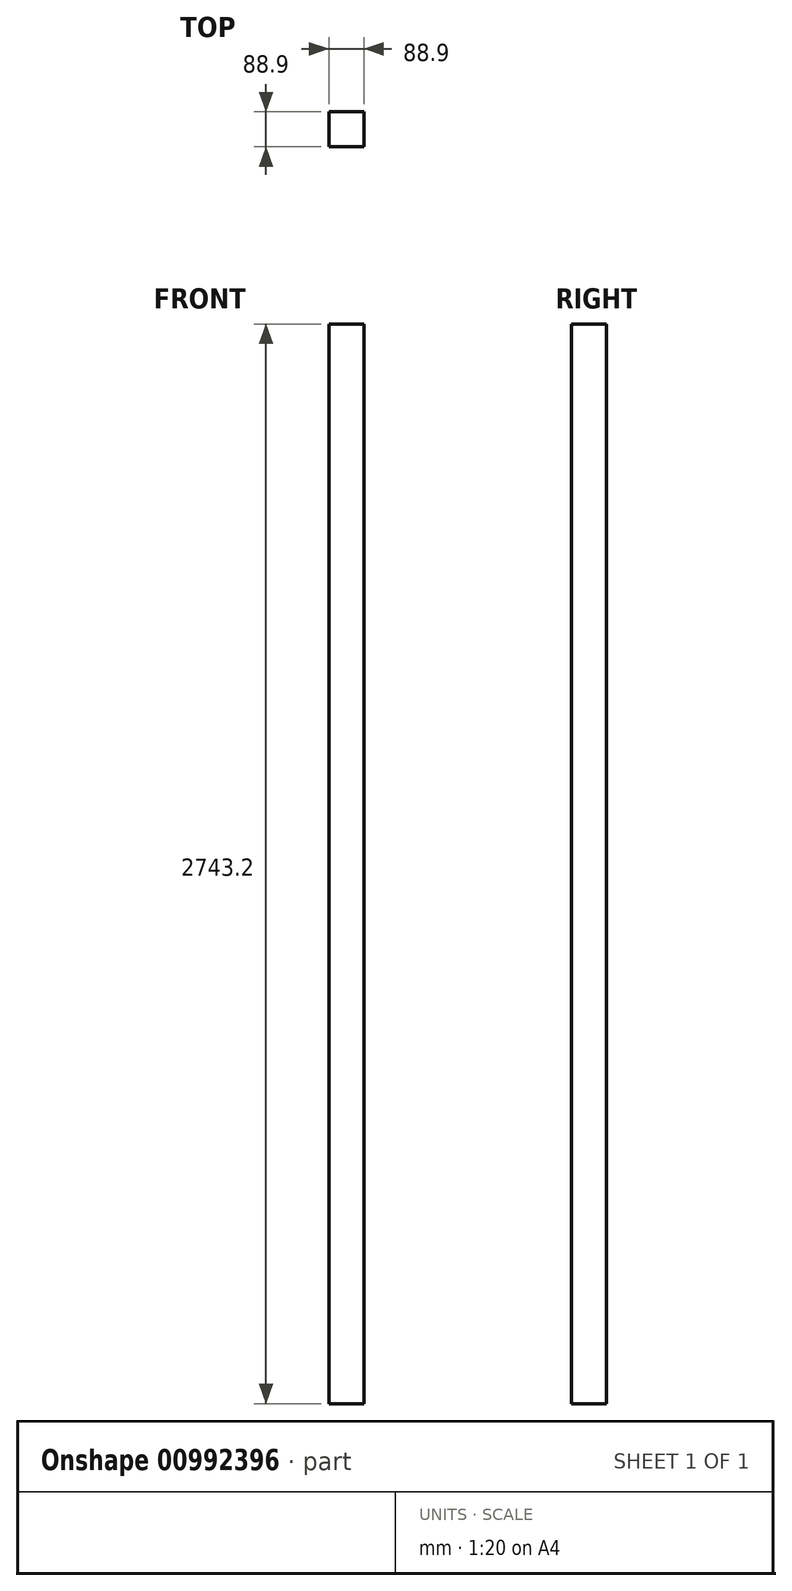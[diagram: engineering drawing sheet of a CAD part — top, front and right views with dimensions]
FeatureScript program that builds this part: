
annotation { "Feature Type Name" : "Feature", "Feature Type Description" : "" }
export const myFeature = defineFeature(function(context is Context, id is Id, definition is map)
    precondition{}
    {
        {
            var Q0;
            Q0=qCreatedBy(makeId("Top.planeOp"),FACE);
            var sketch = newSketch(context, id + "F0", { "sketchPlane" : qUnion([Q0])});
            skLineSegment(sketch, "E0.bottom", {"start": v(44.45, 44.45) * mm, "end": v(-44.45, 44.45) * mm});
            skLineSegment(sketch, "E0.top", {"start": v(44.45, -44.45) * mm, "end": v(-44.45, -44.45) * mm});
            skLineSegment(sketch, "E0.left", {"start": v(44.45, 44.45) * mm, "end": v(44.45, -44.45) * mm});
            skLineSegment(sketch, "E0.right", {"start": v(-44.45, 44.45) * mm, "end": v(-44.45, -44.45) * mm});
            skPoint(sketch, "E0.middle", {"position": v(0, 0) * mm});
            skSolve(sketch);
        }
        {
            var Q0;
            Q0=makeQuery(id+"F0.imprint","IMPRINT",FACE,{"disambiguationData":[TD([[makeQuery(id+"F0.imprint","IMPRINT",EDGE,{"derivedFrom":sQuery(id+"F0.wireOp",EDGE,"E0.bottom")}),1.0]])]});
            extrude(context, id + "F1", {"entities" : qUnion([Q0]), "depth" : 2133.6 * mm, "offsetDistance" : 25.4 * mm, "hasSecondDirection" : true, "secondDirectionOppositeDirection" : true, "secondDirectionDepth" : 609.6 * mm});
        }
    });
